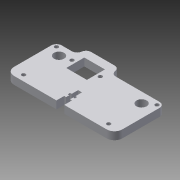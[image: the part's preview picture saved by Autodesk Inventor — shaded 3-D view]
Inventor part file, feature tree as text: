
AUTODESK INVENTOR PART (.ipt)
format: ipt  version: 2013 (Build 170138000, 138)  size: 135,680 bytes
history: native  units: mm
features: extrude x1, sketch x1
ambient origin geometry x8: Origin, YZ Plane, XZ Plane, XY Plane, X Axis, Y Axis, Z Axis, Center Point
bodies: Solid1 (feature_tree)
feature tree (2):
  extrude  "Extrusion1"  [1 undecoded]
  sketch  "Sketch1"  dims[d0=6.0mm d1=0.0mm]
note: 1 required parameter value undecoded (feature->parameter linkage not recoverable at this tier; creation-order binding heuristic only, values carry confidence <= 0.55)
